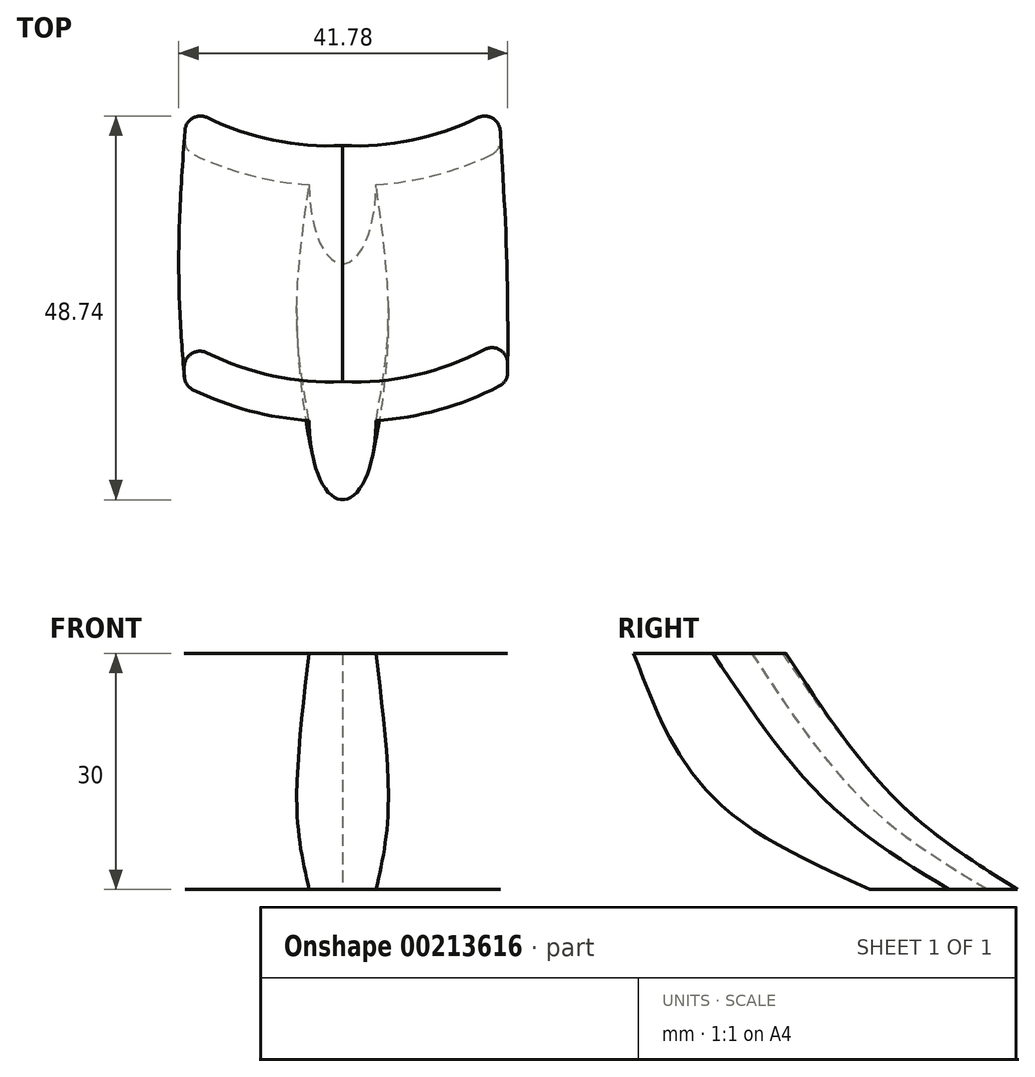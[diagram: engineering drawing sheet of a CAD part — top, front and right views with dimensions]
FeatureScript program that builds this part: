
annotation { "Feature Type Name" : "Feature", "Feature Type Description" : "" }
export const myFeature = defineFeature(function(context is Context, id is Id, definition is map)
    precondition{}
    {
        {
            var Q0;
            Q0=qCreatedBy(makeId("Right.planeOp"),FACE);
            var sketch = newSketch(context, id + "F0", { "sketchPlane" : qUnion([Q0])});
            skLineSegment(sketch, "E0.bottom", {"start": v(0, 0) * mm, "end": v(30, 0) * mm, "construction": true});
            skLineSegment(sketch, "E0.left", {"start": v(0, 0) * mm, "end": v(0, 30) * mm, "construction": true});
            skArc(sketch, "E1", {"start": v(0, 30) * mm, "mid": v(11.66, 11.66) * mm, "end": v(30, 0) * mm});
            skPoint(sketch, "E2", {"position": v(13.08, 10.3) * mm});
            skPoint(sketch, "E3", {"position": v(30, 0) * mm});
            skArc(sketch, "E4", {"start": v(-15, 30) * mm, "mid": v(-3.34, 11.66) * mm, "end": v(15, 0) * mm});
            skSolve(sketch);
        }
        {
            var Q0;
            Q0=sQuery(id+"F0.wireOp",VERTEX,"E1.start");
            var Q1;
            Q1=qCreatedBy(makeId("Top.planeOp"),FACE);
            cPlane(context, id + "F1", {"entities" : qUnion([Q0, Q1]), "cplaneType" : CPlaneType.PLANE_POINT, "offset" : 25 * mm, "width" : 150 * mm, "height" : 150 * mm});
        }
        {
            var Q0;
            Q0=qCreatedBy(id+"F1.planeOp",FACE);
            var sketch = newSketch(context, id + "F2", { "sketchPlane" : qUnion([Q0])});
            skArc(sketch, "E5", {"start": v(-17.21, 3.67) * mm, "mid": v(-8.84, 0.73) * mm, "end": v(0, 0) * mm});
            skArc(sketch, "E6", {"start": v(0, 0) * mm, "mid": v(9.3, 0.83) * mm, "end": v(18.03, 4.1) * mm});
            skArc(sketch, "E7.0", {"start": v(4.25, -4.94) * mm, "mid": v(12.3, -3.56) * mm, "end": v(19.9, -0.58) * mm});
            skArc(sketch, "E7.1", {"start": v(-18.98, -1.04) * mm, "mid": v(-11.8, -3.7) * mm, "end": v(-4.25, -4.94) * mm});
            skEllipticalArc(sketch, "E8", {});
            skPoint(sketch, "E9.visualSharp", {"position": v(-35, 13.03) * mm});
            skPoint(sketch, "E10.visualSharp", {"position": v(35, 13.03) * mm});
            skPoint(sketch, "E11.end.orphan", {"position": v(0, -15) * mm});
            skLineSegment(sketch, "E12", {"start": v(-20.1, 0.76) * mm, "end": v(-20.1, 1.88) * mm});
            skPoint(sketch, "E13.start.orphan", {"position": v(-35, 24.67) * mm});
            skLineSegment(sketch, "E14", {"start": v(20.98, 1.2) * mm, "end": v(20.98, 2.33) * mm});
            skPoint(sketch, "E15.start.orphan", {"position": v(35, 24.67) * mm});
            skPoint(sketch, "E16.visualSharp", {"position": v(20.98, 5.85) * mm});
            skArc(sketch, "E16.filletArc", {"start": v(20.98, 2.33) * mm, "mid": v(20, 4.04) * mm, "end": v(18.03, 4.1) * mm});
            skPoint(sketch, "E17.visualSharp", {"position": v(20.98, 0) * mm});
            skArc(sketch, "E17.filletArc", {"start": v(19.9, -0.58) * mm, "mid": v(20.68, 0.16) * mm, "end": v(20.98, 1.2) * mm});
            skPoint(sketch, "E18.visualSharp", {"position": v(-20.1, 5.29) * mm});
            skArc(sketch, "E18.filletArc", {"start": v(-17.21, 3.67) * mm, "mid": v(-19.16, 3.58) * mm, "end": v(-20.1, 1.88) * mm});
            skPoint(sketch, "E19.visualSharp", {"position": v(-20.1, -0.47) * mm});
            skArc(sketch, "E19.filletArc", {"start": v(-20.1, 0.76) * mm, "mid": v(-19.8, -0.3) * mm, "end": v(-18.98, -1.04) * mm});
            const initialGuessF2  = {"E8": [0, -0.005004295268239853, 0, -1, 0.01, 0.00424685629998106, 4.7062911756630585, 1.576894131516557]};
            skSetInitialGuess(sketch, initialGuessF2);
            skSolve(sketch);
        }
        {
            var Q0;
            Q0=sQuery(id+"F0.wireOp",VERTEX,"E2");
            var Q1;
            Q1=qCreatedBy(makeId("Top.planeOp"),FACE);
            cPlane(context, id + "F3", {"entities" : qUnion([Q0, Q1]), "cplaneType" : CPlaneType.PLANE_POINT, "offset" : 25 * mm, "width" : 150 * mm, "height" : 150 * mm});
        }
        {
            var Q0;
            Q0=qCreatedBy(makeId("Top.planeOp"),FACE);
            var sketch = newSketch(context, id + "F4", { "sketchPlane" : qUnion([Q0])});
            skArc(sketch, "E20", {"start": v(-17.16, 33.54) * mm, "mid": v(-8.8, 30.68) * mm, "end": v(0, 30) * mm});
            skArc(sketch, "E21", {"start": v(0, 30) * mm, "mid": v(8.8, 30.68) * mm, "end": v(17.16, 33.54) * mm});
            skArc(sketch, "E22.0", {"start": v(4.25, 25.04) * mm, "mid": v(11.75, 26.23) * mm, "end": v(18.9, 28.83) * mm});
            skArc(sketch, "E22.1", {"start": v(-18.9, 28.83) * mm, "mid": v(-11.75, 26.23) * mm, "end": v(-4.25, 25.04) * mm});
            skEllipticalArc(sketch, "E23", {});
            skPoint(sketch, "E24.visualSharp", {"position": v(-35, 42.75) * mm});
            skPoint(sketch, "E25.visualSharp", {"position": v(35, 42.75) * mm});
            skPoint(sketch, "E26.end.orphan", {"position": v(0, 15) * mm});
            skLineSegment(sketch, "E27", {"start": v(-20.04, 30.63) * mm, "end": v(-20.04, 31.74) * mm});
            skLineSegment(sketch, "E28", {"start": v(20.04, 30.63) * mm, "end": v(20.04, 31.74) * mm});
            skPoint(sketch, "E29.start.orphan", {"position": v(-35, 54.09) * mm});
            skPoint(sketch, "E30.start.orphan", {"position": v(35, 54.09) * mm});
            skPoint(sketch, "E31.visualSharp", {"position": v(-20.04, 35.13) * mm});
            skArc(sketch, "E31.filletArc", {"start": v(-17.16, 33.54) * mm, "mid": v(-19.1, 33.44) * mm, "end": v(-20.04, 31.74) * mm});
            skPoint(sketch, "E32.visualSharp", {"position": v(-20.04, 29.4) * mm});
            skArc(sketch, "E32.filletArc", {"start": v(-20.04, 30.63) * mm, "mid": v(-19.73, 29.57) * mm, "end": v(-18.9, 28.83) * mm});
            skPoint(sketch, "E33.visualSharp", {"position": v(20.04, 29.4) * mm});
            skArc(sketch, "E33.filletArc", {"start": v(18.9, 28.83) * mm, "mid": v(19.73, 29.57) * mm, "end": v(20.04, 30.63) * mm});
            skPoint(sketch, "E34.visualSharp", {"position": v(20.04, 35.13) * mm});
            skArc(sketch, "E34.filletArc", {"start": v(20.04, 31.74) * mm, "mid": v(19.1, 33.44) * mm, "end": v(17.16, 33.54) * mm});
            const initialGuessF4  = {"E23": [0, 0.02499464675454087, 0, -1, 0.01, 0.00424685629998106, 4.70820626848456, 1.5749790386950258]};
            skSetInitialGuess(sketch, initialGuessF4);
            skSolve(sketch);
        }
        {
            var Q0;
            Q0=qCreatedBy(id+"F3.planeOp",FACE);
            var sketch = newSketch(context, id + "F5", { "sketchPlane" : qUnion([Q0])});
            skArc(sketch, "E35", {"start": v(-17.86, 19.24) * mm, "mid": v(-9.2, 16.06) * mm, "end": v(0, 15.24) * mm});
            skArc(sketch, "E36", {"start": v(0, 15.24) * mm, "mid": v(9.2, 16.06) * mm, "end": v(17.86, 19.24) * mm});
            skArc(sketch, "E37.0", {"start": v(5.8, 10.44) * mm, "mid": v(12.94, 11.86) * mm, "end": v(19.7, 14.56) * mm});
            skArc(sketch, "E37.1", {"start": v(-19.7, 14.56) * mm, "mid": v(-12.94, 11.86) * mm, "end": v(-5.8, 10.44) * mm});
            skEllipticalArc(sketch, "E38", {});
            skPoint(sketch, "E39.visualSharp", {"position": v(-35, 28.28) * mm});
            skPoint(sketch, "E40.visualSharp", {"position": v(35, 28.28) * mm});
            skLineSegment(sketch, "E41", {"start": v(5.8, 10.02) * mm, "end": v(52.16, 8.22) * mm, "construction": true});
            skPoint(sketch, "E42.end.orphan", {"position": v(0, -3.4) * mm});
            skLineSegment(sketch, "E43", {"start": v(-20.8, 16.35) * mm, "end": v(-20.8, 17.47) * mm});
            skLineSegment(sketch, "E44", {"start": v(20.8, 16.35) * mm, "end": v(20.8, 17.47) * mm});
            skPoint(sketch, "E45.start.orphan", {"position": v(-35, 39.91) * mm});
            skPoint(sketch, "E46.start.orphan", {"position": v(35, 39.91) * mm});
            skPoint(sketch, "E47.visualSharp", {"position": v(-20.8, 20.97) * mm});
            skArc(sketch, "E47.filletArc", {"start": v(-17.86, 19.24) * mm, "mid": v(-19.82, 19.18) * mm, "end": v(-20.8, 17.47) * mm});
            skPoint(sketch, "E48.visualSharp", {"position": v(-20.8, 15.14) * mm});
            skArc(sketch, "E48.filletArc", {"start": v(-20.8, 16.35) * mm, "mid": v(-20.5, 15.3) * mm, "end": v(-19.7, 14.56) * mm});
            skPoint(sketch, "E49.visualSharp", {"position": v(20.8, 15.14) * mm});
            skArc(sketch, "E49.filletArc", {"start": v(19.7, 14.56) * mm, "mid": v(20.5, 15.3) * mm, "end": v(20.8, 16.35) * mm});
            skPoint(sketch, "E50.visualSharp", {"position": v(20.8, 20.97) * mm});
            skArc(sketch, "E50.filletArc", {"start": v(20.8, 17.47) * mm, "mid": v(19.82, 19.18) * mm, "end": v(17.86, 19.24) * mm});
            const initialGuessF5  = {"E38": [0, 0.010239718219022108, 0, -1, 0.013648054886290902, 0.005796132787633201, 4.69803207104009, 1.5851532361394944]};
            skSetInitialGuess(sketch, initialGuessF5);
            skSolve(sketch);
        }
        {
            var Q0;
            Q0=makeQuery(id+"F2.imprint","IMPRINT",FACE,{"disambiguationData":[TD([[makeQuery(id+"F2.imprint","IMPRINT",EDGE,{"derivedFrom":sQuery(id+"F2.wireOp",EDGE,"E5")}),-1.0]])]});
            var Q1;
            Q1=makeQuery(id+"F5.imprint","IMPRINT",FACE,{"disambiguationData":[TD([[makeQuery(id+"F5.imprint","IMPRINT",EDGE,{"derivedFrom":sQuery(id+"F5.wireOp",EDGE,"E35")}),-1.0]])]});
            var Q2;
            Q2=makeQuery(id+"F4.imprint","IMPRINT",FACE,{"disambiguationData":[TD([[makeQuery(id+"F4.imprint","IMPRINT",EDGE,{"derivedFrom":sQuery(id+"F4.wireOp",EDGE,"E20")}),-1.0]])]});
            loft(context, id + "F6", {"sheetProfilesArray" : [{ "sheetProfileEntities" : qUnion([Q0]) }, { "sheetProfileEntities" : qUnion([Q1]) }, { "sheetProfileEntities" : qUnion([Q2]) }]});
        }
    });
